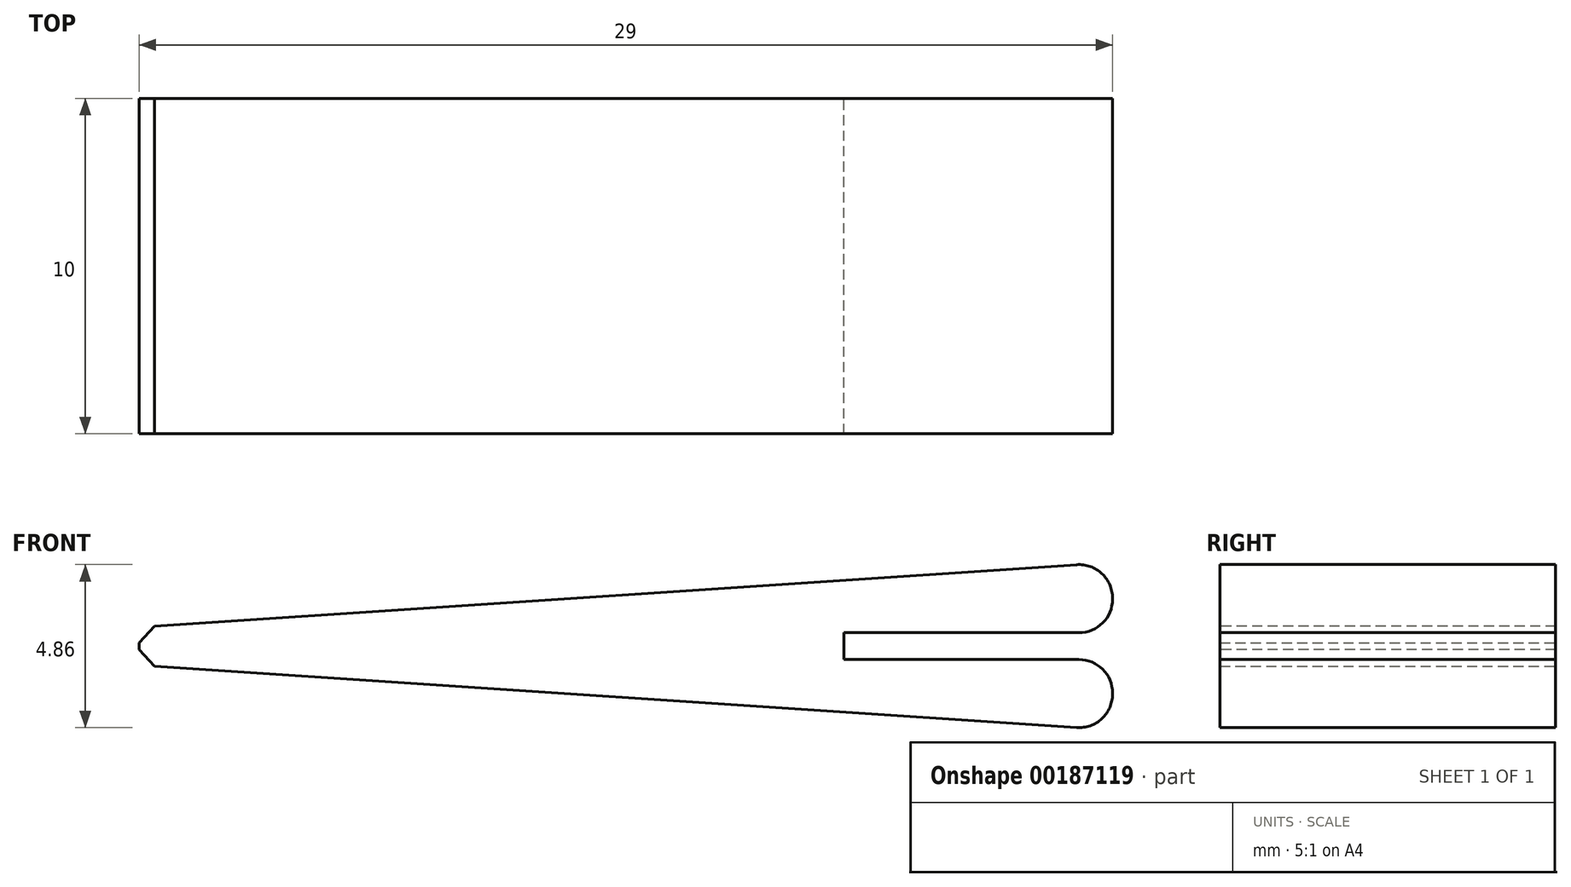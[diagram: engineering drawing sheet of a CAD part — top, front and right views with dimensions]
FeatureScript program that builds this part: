
annotation { "Feature Type Name" : "Feature", "Feature Type Description" : "" }
export const myFeature = defineFeature(function(context is Context, id is Id, definition is map)
    precondition{}
    {
        {
            var Q0;
            Q0=qCreatedBy(makeId("Front.planeOp"),FACE);
            var sketch = newSketch(context, id + "F0", { "sketchPlane" : qUnion([Q0])});
            skLineSegment(sketch, "E0.bottom", {"start": v(15, 2.5) * mm, "end": v(-15, 2.5) * mm});
            skLineSegment(sketch, "E0.top", {"start": v(15, -2.5) * mm, "end": v(-15, -2.5) * mm});
            skLineSegment(sketch, "E0.left", {"start": v(15, 2.5) * mm, "end": v(15, -2.5) * mm});
            skLineSegment(sketch, "E0.right", {"start": v(-15, 2.5) * mm, "end": v(-15, -2.5) * mm});
            skPoint(sketch, "E0.middle", {"position": v(0, 0) * mm});
            skLineSegment(sketch, "E1", {"start": v(-15, 0) * mm, "end": v(-15, -0.5) * mm});
            skLineSegment(sketch, "E2", {"start": v(-15, 0) * mm, "end": v(-15, 0.5) * mm});
            skLineSegment(sketch, "E3", {"start": v(-15, 0.5) * mm, "end": v(15, 2.5) * mm});
            skLineSegment(sketch, "E4", {"start": v(-15, -0.5) * mm, "end": v(15, -2.5) * mm});
            skLineSegment(sketch, "E5", {"start": v(15, 0) * mm, "end": v(15, -0.4) * mm});
            skLineSegment(sketch, "E6", {"start": v(15, 0) * mm, "end": v(15, 0.4) * mm});
            skLineSegment(sketch, "E7", {"start": v(15, 0.4) * mm, "end": v(7, 0.4) * mm});
            skLineSegment(sketch, "E8", {"start": v(7, 0.4) * mm, "end": v(7, -0.4) * mm});
            skLineSegment(sketch, "E9", {"start": v(7, -0.4) * mm, "end": v(15, -0.4) * mm});
            skLineSegment(sketch, "E10", {"start": v(-15, 0) * mm, "end": v(-14, 0) * mm});
            skLineSegment(sketch, "E11", {"start": v(-14, 0) * mm, "end": v(-14, -2.5) * mm});
            skLineSegment(sketch, "E12", {"start": v(-14, 0) * mm, "end": v(-14, 2.5) * mm});
            skLineSegment(sketch, "E13", {"start": v(-14, 0) * mm, "end": v(-14, 0.57) * mm});
            skLineSegment(sketch, "E14", {"start": v(-14, 0) * mm, "end": v(-14, -0.57) * mm});
            skSolve(sketch);
        }
        {
            var Q0;
            {var subQ8=sQuery(id+"F0.wireOp",EDGE,"E7");Q0=makeQuery(id+"F0.imprint","IMPRINT",FACE,{"disambiguationData":[TD([[makeQuery(id+"F0.imprint","IMPRINT",EDGE,{"derivedFrom":subQ8}),-1.0]])]});}
            extrude(context, id + "F1", {"entities" : qUnion([Q0]), "depth" : 10 * mm});
        }
        {
            var Q0;
            Q0=makeQuery(id+"F1.opExtrude","SWEPT_EDGE",EDGE,{"disambiguationData":[OSD([sQuery(id+"F0.wireOp",EDGE,"E0.left"),sQuery(id+"F0.wireOp",EDGE,"E5"),sQuery(id+"F0.wireOp",EDGE,"E9")])]});
            var Q1;
            Q1=makeQuery(id+"F1.opExtrude","SWEPT_EDGE",EDGE,{"disambiguationData":[OSD([sQuery(id+"F0.wireOp",EDGE,"E0.left"),sQuery(id+"F0.wireOp",EDGE,"E6"),sQuery(id+"F0.wireOp",EDGE,"E7")])]});
            var Q2;
            Q2=makeQuery(id+"F1.opExtrude","SWEPT_EDGE",EDGE,{"disambiguationData":[OSD([sQuery(id+"F0.wireOp",EDGE,"E0.top"),sQuery(id+"F0.wireOp",EDGE,"E0.left"),sQuery(id+"F0.wireOp",EDGE,"E4")])]});
            var Q3;
            Q3=makeQuery(id+"F1.opExtrude","SWEPT_EDGE",EDGE,{"disambiguationData":[OSD([sQuery(id+"F0.wireOp",EDGE,"E0.bottom"),sQuery(id+"F0.wireOp",EDGE,"E0.left"),sQuery(id+"F0.wireOp",EDGE,"E3")])]});
            fillet(context, id + "F2", {"entities" : qUnion([Q0, Q1, Q2, Q3]), "radius" : 1 * mm, "tangentPropagation" : true, "allowEdgeOverflow" : false});
        }
        {
            var Q0;
            Q0=makeQuery(id+"F1.opExtrude","SWEPT_EDGE",EDGE,{"disambiguationData":[OSD([sQuery(id+"F0.wireOp",EDGE,"E3"),sQuery(id+"F0.wireOp",EDGE,"E12"),sQuery(id+"F0.wireOp",EDGE,"E13")])]});
            var Q1;
            Q1=makeQuery(id+"F1.opExtrude","SWEPT_EDGE",EDGE,{"disambiguationData":[OSD([sQuery(id+"F0.wireOp",EDGE,"E4"),sQuery(id+"F0.wireOp",EDGE,"E11"),sQuery(id+"F0.wireOp",EDGE,"E14")])]});
            chamfer(context, id + "F3", {"entities" : qUnion([Q0, Q1]), "width" : .5 * mm, "tangentPropagation" : true});
        }
    });
